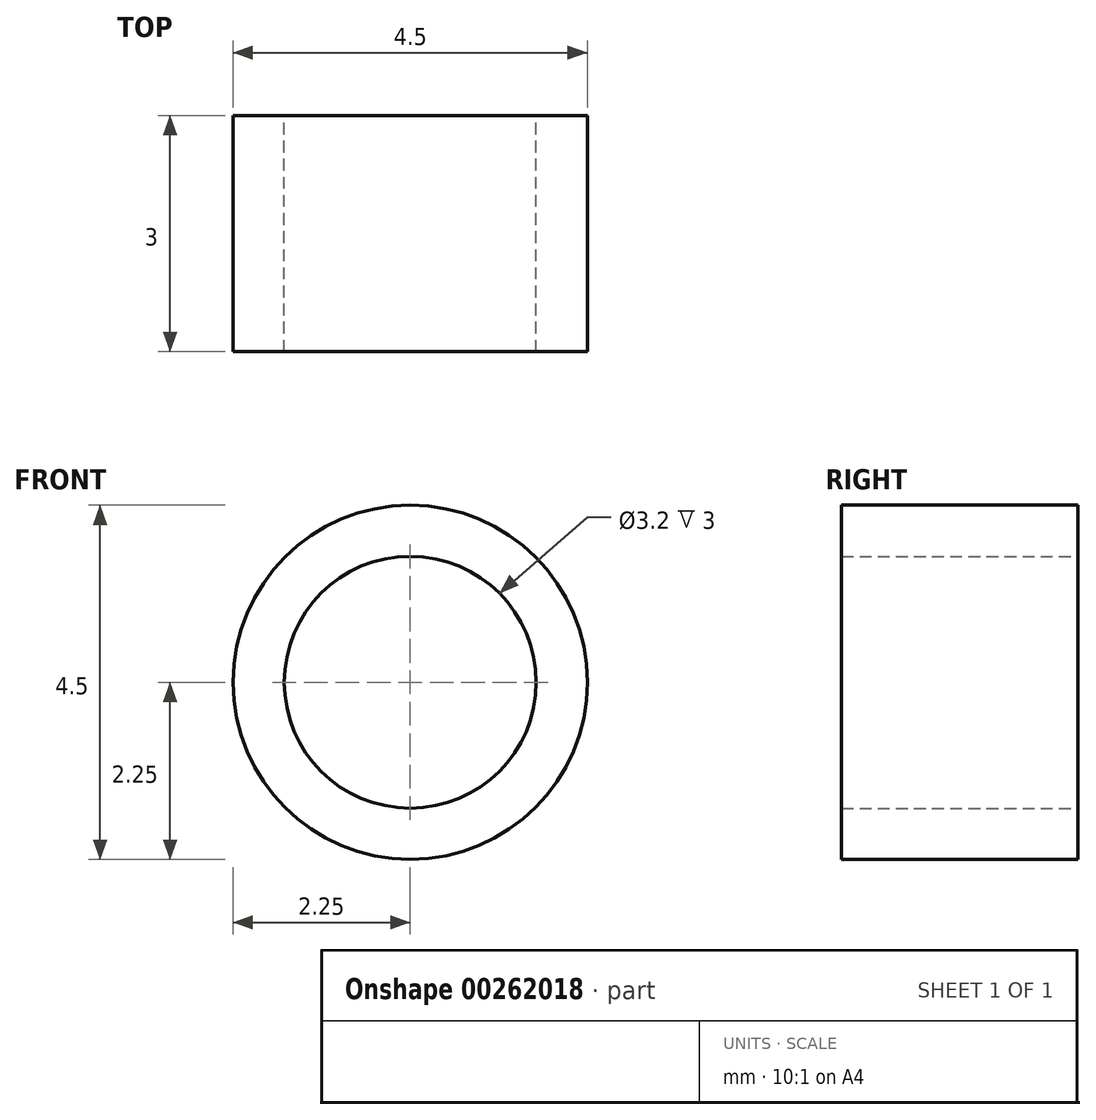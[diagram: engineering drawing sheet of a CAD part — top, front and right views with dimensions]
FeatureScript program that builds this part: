
annotation { "Feature Type Name" : "Feature", "Feature Type Description" : "" }
export const myFeature = defineFeature(function(context is Context, id is Id, definition is map)
    precondition{}
    {
        {
            assignVariable(context, id + "F0", {"name" : "Hieght", "anyValue" : 3});
        }
        {
            var Q0;
            Q0=qCreatedBy(makeId("Front.planeOp"),FACE);
            var sketch = newSketch(context, id + "F1", { "sketchPlane" : qUnion([Q0])});
            skCircle(sketch, "E0", {"center": v(0, 0) * mm, "radius": 1.6 * mm});
            skCircle(sketch, "E1", {"center": v(0, 0) * mm, "radius": 2.25 * mm});
            skSolve(sketch);
        }
        {
            var Q0;
            Q0=makeQuery(id+"F1.imprint","IMPRINT",FACE,{"disambiguationData":[TD([[makeQuery(id+"F1.imprint","IMPRINT",EDGE,{"derivedFrom":sQuery(id+"F1.wireOp",EDGE,"E0")}),-1.0]])]});
            extrude(context, id + "F2", {"entities" : qUnion([Q0]), "depth" : getVariable(context, 'Hieght') * mm});
        }
    });
